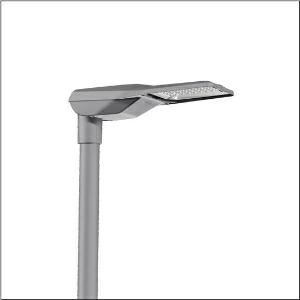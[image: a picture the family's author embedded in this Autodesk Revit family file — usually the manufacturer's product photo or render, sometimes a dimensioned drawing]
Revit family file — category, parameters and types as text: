
# Revit family: streetlight_sl_21_iq_mini___st1_5a_5xe2p31d08hb_3c75
name_source: partatom
category: Lighting Fixtures
units: mm (PartAtom-declared; Revit-internal decimal feet)

## family parameters
Cut with Voids When Loaded = No
Host = Face
Light Source = No
Part Type = Normal
Room Calculation Point = No
Round Connector Dimension = Use Diameter
Shared = No

## types (1)
- --- (1 x LED, 9290 lm, 70.9 W, 3000K)
    Apparent Load = 71 VA
    CIE Flux Codes = 22 53 95 100 100
    Color Rendering = 70
    Color Temperature = 3000K
    Default Elevation = 1800 mm
    Description = Streetlight SL 21 iQ mini, mast luminaire, primary light control with lens, of PMMA, primary optical cover: cover, of toughened safety glass, transparent, light distribution: ST1.5a, light emission: direct distribution, primary light characteristic: asymmetric, installation type: post-top, side-entry, LED, High Power LED, rated luminous flux: 9.290lm, luminous efficacy: 131lm/W, light colour: 730, colour temperature: 3000K, control: Auto-Match, Temp-Guard, Lumen-Switch, Night-Set, Smart-Wire, Light-Fading, Desk-Remote (wireless, voltage-free reading and setting of iQ features in the workshop via application-optimized NFC function/RFID function), optimised constant luminous flux control (CLO 2.0), presetting dimming linear, mains connection: 220..240V, AC, 50/60Hz, start of lifetime: 71W, end of service life: 75W, reduction: 31W, luminaire housing, of diecast aluminium, powder-coated, Siteco® metallic grey (DB 702S), corrosivity category C5 mid according to DIN EN ISO 12944, please order mast flange separately, inclination adjustable: 0°, 5°, 10°, 15°, sealing non-destructively replaceable, multi-level sealing system, length: 628mm, width: 235mm, height: 110mm, mast flange for spigot size: 42mm (side-entry): 5XC10008XM4, 60/48mm (side-entry/post-top): 5XC10108XM2, 76/60mm (side-entry/post-top): 5XC10108XM1, protection rating (complete): IP66, insulation class (complete): insulation class II (safety insulation), certification: CE, ENEC, ENEC+, VDE, impact resistance: IK09, permissible operating ambient temperature for outdoor applications: -40..+50°C, standard-compliant lighting for roads and squares, packaging unit: 1 piece

Light Distribution: ST1.5a
    Height = 110 mm
    Lamp = 1 x LED
    Lamp Light Flux = 9290 lm
    Lamp Power = 70.9 W
    Lamp count = 1
    Length = 625 mm
    Luminous efficacy = 131 lm/W
    Manufacturer = Siteco
    ModVariant = No
    Model = 5XE2P31D08HB
    Number of Poles = 1
    OnlyDefault = Yes
    Power Factor = 1
    Product Name = Streetlight SL 21 iQ mini | ST1.5a
    Product group = mast luminaire | pylon top
    ProductGroupID = 6100
    Protection Class = Protection class II
    Protection Degree = IP 66
    RLX_Detail_Level = 1
    RLX_Emergency_Light_Flux = 0 lm
    RLX_Emergency_Type = 0
    RLX_Emergency_Type_DB = No
    RlxData = <blob elided: 95785 chars, md5=eea39639>
    Socket = socket
    Standby Power = 0 W
    System Light Flux = 9290 lm
    System Power = 71 W
    Type Comments = factory setting: luminous flux: 100 % | dim-lin: 254 | 711 mA
    Type Image = l_1003519.jpg
    URL = http://relux.com
    VarID = @adj_089431
    Voltage = 0 V
    Weight = 0.00 kg
    Width = 234 mm

## geometry (parser evidence)
native form markers: Blend x4, Sweep x11
no freeform markers — native parametric forms only
